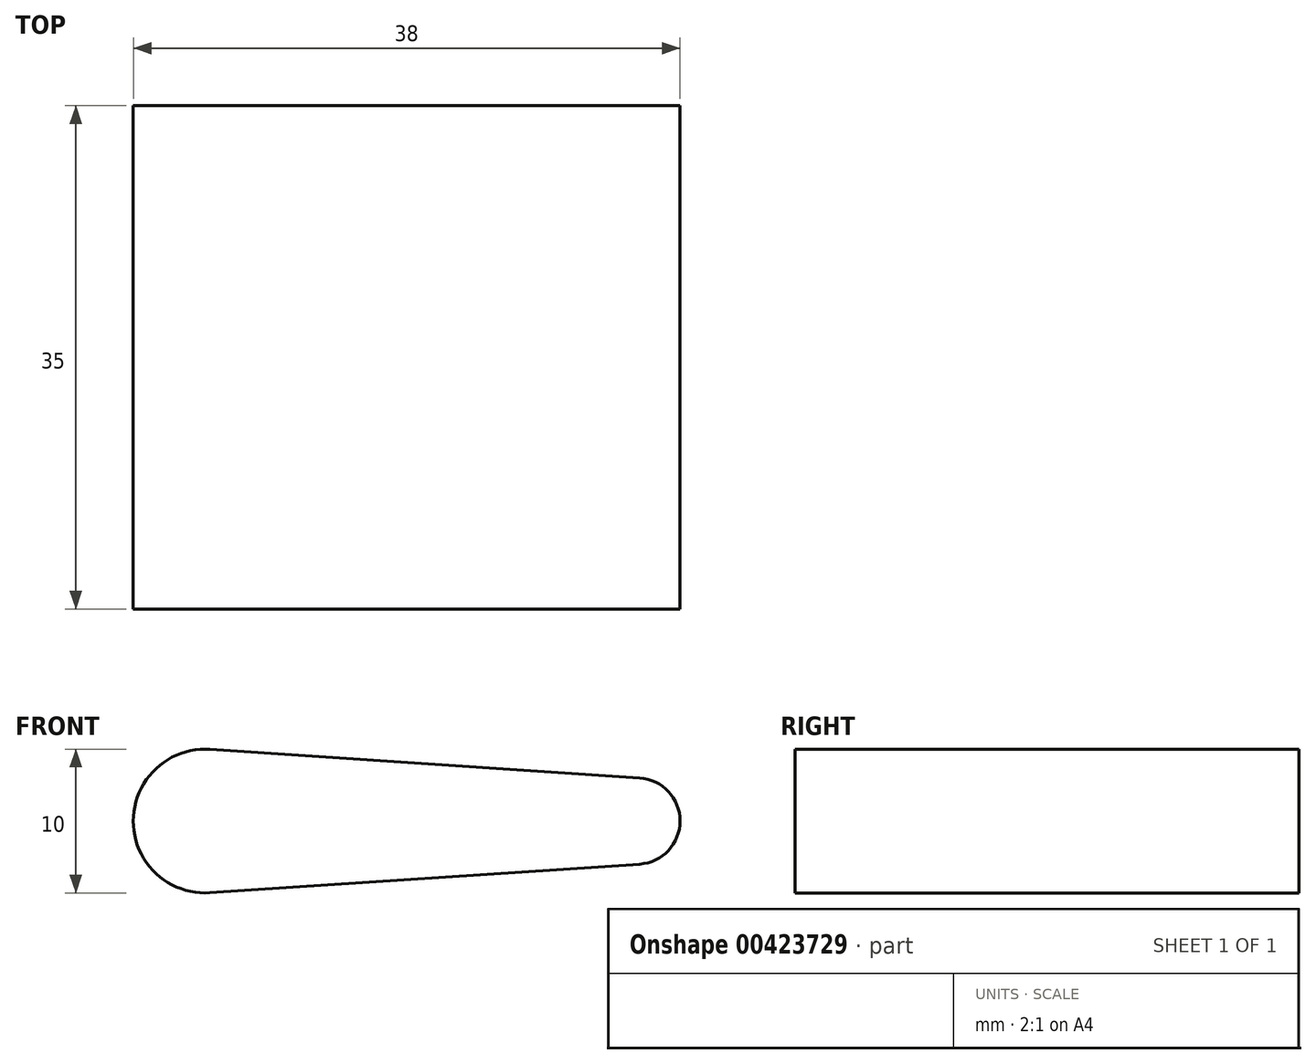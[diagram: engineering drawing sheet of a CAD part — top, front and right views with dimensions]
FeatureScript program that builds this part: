
annotation { "Feature Type Name" : "Feature", "Feature Type Description" : "" }
export const myFeature = defineFeature(function(context is Context, id is Id, definition is map)
    precondition{}
    {
        {
            var Q0;
            Q0=qCreatedBy(makeId("Front.planeOp"),FACE);
            var sketch = newSketch(context, id + "F0", { "sketchPlane" : qUnion([Q0])});
            skLineSegment(sketch, "E0", {"start": v(-50.8, 0) * mm, "end": v(49.2, 0) * mm});
            skLineSegment(sketch, "E1", {"start": v(-50.8, 0) * mm, "end": v(-35.8, 0) * mm});
            skArc(sketch, "E2", {"start": v(-37.1, 14.94) * mm, "mid": v(-50.8, -0.26) * mm, "end": v(-36.58, -14.98) * mm});
            skLineSegment(sketch, "E3", {"start": v(49.2, 0) * mm, "end": v(29.2, 0) * mm});
            skArc(sketch, "E4", {"start": v(29.34, -2) * mm, "mid": v(31.2, 0) * mm, "end": v(29.34, 2) * mm});
            skArc(sketch, "E5", {"start": v(29.4, -3) * mm, "mid": v(32.2, 0) * mm, "end": v(29.4, 3) * mm});
            skLineSegment(sketch, "E6", {"start": v(29.2, 0) * mm, "end": v(6.7, 0) * mm});
            skLineSegment(sketch, "E7", {"start": v(29.2, 0) * mm, "end": v(-0.8, 0) * mm});
            skArc(sketch, "E8", {"start": v(6.94, 3.5) * mm, "mid": v(3.2, 0) * mm, "end": v(6.94, -3.5) * mm});
            skArc(sketch, "E9", {"start": v(-0.46, 4.99) * mm, "mid": v(-5.8, 0) * mm, "end": v(-0.46, -4.99) * mm});
            skLineSegment(sketch, "E10", {"start": v(6.94, 3.5) * mm, "end": v(29.34, 2) * mm});
            skLineSegment(sketch, "E11", {"start": v(6.94, -3.5) * mm, "end": v(29.34, -2) * mm});
            skLineSegment(sketch, "E12", {"start": v(-0.46, 4.99) * mm, "end": v(29.4, 3) * mm});
            skLineSegment(sketch, "E13", {"start": v(-0.46, -4.99) * mm, "end": v(29.4, -3) * mm});
            skArc(sketch, "E14", {"start": v(45.68, -4.78) * mm, "mid": v(49.2, -0.08) * mm, "end": v(45.83, 4.73) * mm});
            skArc(sketch, "E15", {"start": v(45.83, 4.73) * mm, "mid": v(4.9, 14.19) * mm, "end": v(-37.1, 14.94) * mm});
            skArc(sketch, "E16", {"start": v(-36.58, -14.98) * mm, "mid": v(5, -13.5) * mm, "end": v(45.68, -4.78) * mm});
            skSolve(sketch);
        }
        {
            var Q0;
            {var subQ4=sQuery(id+"F0.wireOp",EDGE,"E11");Q0=makeQuery(id+"F0.imprint","IMPRINT",FACE,{"disambiguationData":[TD([[makeQuery(id+"F0.imprint","IMPRINT",EDGE,{"derivedFrom":subQ4}),1.0]])]});}
            var Q1;
            {var subQ4=sQuery(id+"F0.wireOp",EDGE,"E10");Q1=makeQuery(id+"F0.imprint","IMPRINT",FACE,{"disambiguationData":[TD([[makeQuery(id+"F0.imprint","IMPRINT",EDGE,{"derivedFrom":subQ4}),-1.0]])]});}
            var Q2;
            {var subQ4=sQuery(id+"F0.wireOp",EDGE,"E11");Q2=makeQuery(id+"F0.imprint","IMPRINT",FACE,{"disambiguationData":[TD([[makeQuery(id+"F0.imprint","IMPRINT",EDGE,{"derivedFrom":subQ4}),-1.0]])]});}
            var Q3;
            {var subQ0=sQuery(id+"F0.wireOp",EDGE,"E10");Q3=makeQuery(id+"F0.imprint","IMPRINT",FACE,{"disambiguationData":[TD([[makeQuery(id+"F0.imprint","IMPRINT",EDGE,{"derivedFrom":subQ0}),1.0]])]});}
            extrude(context, id + "F1", {"entities" : qUnion([Q0, Q1, Q2, Q3]), "oppositeDirection" : true, "depth" : 35 * mm});
        }
    });
